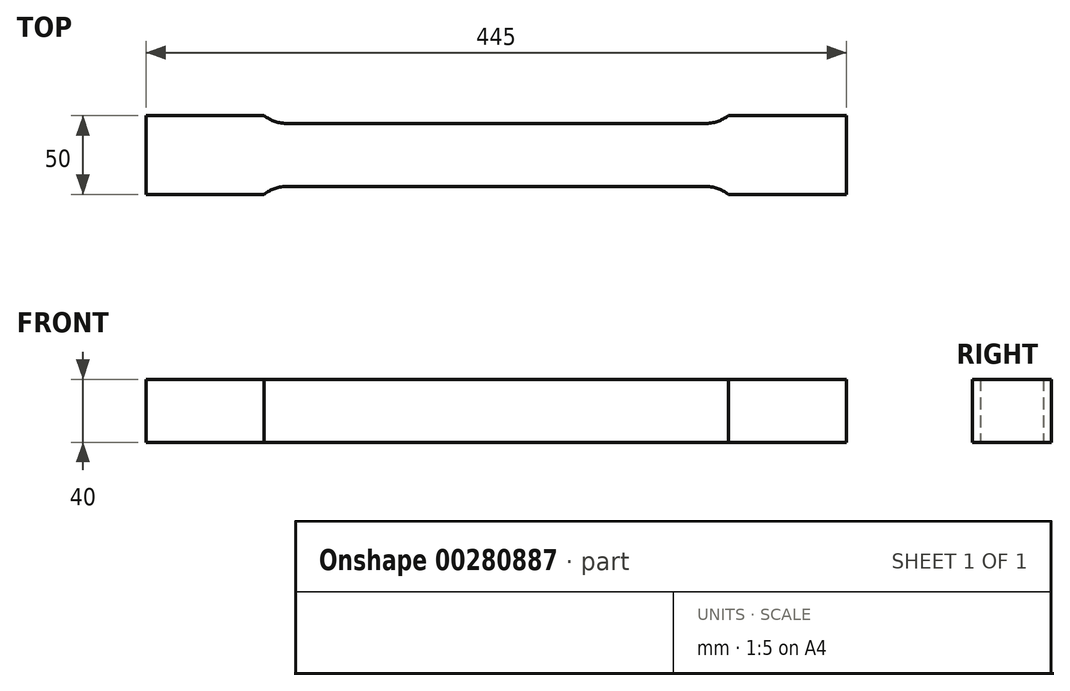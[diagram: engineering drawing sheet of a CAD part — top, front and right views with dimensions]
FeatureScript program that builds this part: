
annotation { "Feature Type Name" : "Feature", "Feature Type Description" : "" }
export const myFeature = defineFeature(function(context is Context, id is Id, definition is map)
    precondition{}
    {
        {
            var Q0;
            Q0=qCreatedBy(makeId("Top.planeOp"),FACE);
            var sketch = newSketch(context, id + "F0", { "sketchPlane" : qUnion([Q0])});
            skLineSegment(sketch, "E0", {"start": v(0, 20) * mm, "end": v(132.5, 20) * mm});
            skArc(sketch, "E1", {"start": v(132.5, 20) * mm, "mid": v(140.4, 21.28) * mm, "end": v(147.5, 25) * mm});
            skLineSegment(sketch, "E2", {"start": v(147.5, 25) * mm, "end": v(222.5, 25) * mm});
            skLineSegment(sketch, "E3", {"start": v(222.5, 25) * mm, "end": v(222.5, 0) * mm});
            skArc(sketch, "E4.MirrorCS", {"start": v(132.5, -20) * mm, "mid": v(140.4, -21.28) * mm, "end": v(147.5, -25) * mm});
            skLineSegment(sketch, "E5.MirrorCS", {"start": v(147.5, -25) * mm, "end": v(222.5, -25) * mm});
            skLineSegment(sketch, "E6.MirrorCS", {"start": v(0, -20) * mm, "end": v(132.5, -20) * mm});
            skLineSegment(sketch, "E7.MirrorCS", {"start": v(222.5, -25) * mm, "end": v(222.5, 0) * mm});
            skLineSegment(sketch, "E8.MirrorCS", {"start": v(-222.5, -25) * mm, "end": v(-222.5, 0) * mm});
            skLineSegment(sketch, "E9.MirrorCS", {"start": v(0, -20) * mm, "end": v(-132.5, -20) * mm});
            skLineSegment(sketch, "E10.MirrorCS", {"start": v(0, 20) * mm, "end": v(-132.5, 20) * mm});
            skArc(sketch, "E11.MirrorCS", {"start": v(-132.5, 20) * mm, "mid": v(-140.4, 21.28) * mm, "end": v(-147.5, 25) * mm});
            skLineSegment(sketch, "E12.MirrorCS", {"start": v(-147.5, 25) * mm, "end": v(-222.5, 25) * mm});
            skArc(sketch, "E13.MirrorCS", {"start": v(-132.5, -20) * mm, "mid": v(-140.4, -21.28) * mm, "end": v(-147.5, -25) * mm});
            skLineSegment(sketch, "E14.MirrorCS", {"start": v(-222.5, 25) * mm, "end": v(-222.5, 0) * mm});
            skLineSegment(sketch, "E15.MirrorCS", {"start": v(-147.5, -25) * mm, "end": v(-222.5, -25) * mm});
            skSolve(sketch);
        }
        {
            var Q0;
            Q0 = qSketchRegion(id + "F0", true);
            extrude(context, id + "F1", {"entities" : qUnion([Q0]), "endBound" : BoundingType.SYMMETRIC, "depth" : 40 * mm});
        }
    });
